# Revit family: EDLR-E2-195-xxxx-8xx-W-EDS3
name_source: partatom
category: Oprawy oświetleniowe
revit_build: Autodesk Revit 2017 (Build: 20190507_1515(x64)
units: mm (PartAtom-declared; Revit-internal decimal feet)

## family parameters
Numer OmniClass = 23.80.70.11
Obiekt nadrzędny = Powierzchnia
Punkt obliczania pomieszczeń = Nie
Tnij formami wycięć po wczytaniu = Tak
Typ części = Normalny
Tytuł OmniClass = Luminaries for Internal Lighting
Współdzielony = Nie
Wymiar okrągłego złącza = Użyj średnicy
Źródło światła = Tak

## types (4) — shared parameters
Emituj kształt widoczny w renderingu = Nie
Emituj ze średnicy okręgu = 180 mm  [stored 0.590551 ft]
Filtr koloru = 16777215
Kod zespołu = D5020200
Lampa = LED
Odchylenie kierunku = 90.00°
Plik sieci fotometrycznej = EDLR-E2 195_1100-840 W.IES
Producent = RIDI Leuchten GmbH
URL = www.ridi.de
Zmiana temperatury barwowej przyciemniania lampy = <Brak>
brand = RIDI
conformity mark = CE
electrical safety class = 1
height = 65 mm  [stored 0.213255 ft]
ingress protection (IP) code = IP20
length = 195 mm  [stored 0.639764 ft]
nominal frequency = 50-60Hz
nominal voltage = 230
voltage type (AC, DC, UC) = AC
width = 195 mm  [stored 0.639764 ft]
zero-valued in all types: Domyślna rzędna

## per-type parameters (varying)
| type | Model | Obciążenie pozorne | rated input power | weight |
| EDLR-E2 195/1100-830 W-EDS3 | 0321512//377 | 9 VA | 9 | 0.8kg |
| EDLR-E2 195/1100-840 W-EDS3 | 0321511//377 | 9 VA | 9 | 0.8kg |
| EDLR-E2 195/2000-830 W-EDS3 | 0321514//377 | 16 VA | 16 | 0.836kg |
| EDLR-E2 195/2000-840 W-EDS3 | 0321513//377 | 16 VA | 16 | 0.836kg |

note: column(s) folded — value = type name in every type: product name

note: [stored X ft] marks values corroborated as IEEE doubles in the binary element streams (Revit-internal decimal feet)
